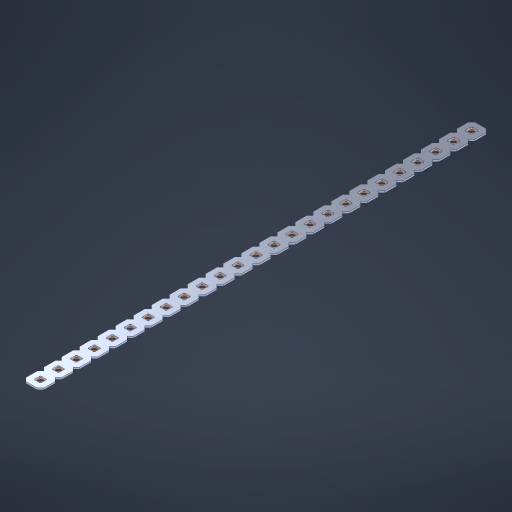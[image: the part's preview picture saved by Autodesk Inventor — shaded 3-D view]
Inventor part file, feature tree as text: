
AUTODESK INVENTOR PART (.ipt)
format: ipt  version: 2023 (Build 270158000, 158)  size: 579,072 bytes
history: native  units: in
note: dims shown in document units (in); Inventor stores cm internally (conversion verified against a paired STEP export)
features: other x26, extrude x24, sketch x2, pattern_linear x1
ambient origin geometry x8: Origin, YZ Plane, XZ Plane, XY Plane, X Axis, Y Axis, Z Axis, Center Point
bodies: Solid1 (feature_tree), Body (feature_tree)
feature tree (53):
  pattern_linear  "Rectangular Pattern1"  Spacing1=0.09in  [1 undecoded]
  sketch  "Sketch1"  dims[d1=0.5in]
  sketch  "Sketch2"  dims[d2=0.182in d3=0.09in d4=0.09in d5=0.09in d6=0.09in d7=0.09in d8=0.09in d9=0.09in d10=0.09in d11=0.02in d13=0.0in d14=0.172in d15=0.0625in d16=0.0in d19=0.5in d22=0.5in]
  other  "Srf1"
  other  "Srf126"
  other  "Srf127"
  other  "Srf128"
  other  "Srf129"
  other  "Srf130"
  other  "Srf131"
  other  "Srf250"
  other  "Srf251"
  other  "Srf252"
  other  "Srf253"
  other  "Srf254"
  other  "Srf255"
  other  "Srf256"
  other  "Srf257"
  other  "Srf258"
  other  "Srf259"
  other  "Srf260"
  other  "Srf261"
  other  "Srf262"
  other  "Srf263"
  other  "Srf264"
  other  "Srf265"
  other  "Srf266"
  other  "Srf267"
  other  "Circle"
  extrude  "ExtrusionSrf126"  Depth=0.09in
  extrude  "ExtrusionSrf127"  Depth=0.09in
  extrude  "ExtrusionSrf128"  Depth=0.09in
  extrude  "ExtrusionSrf129"  Depth=0.09in
  extrude  "ExtrusionSrf130"  Depth=0.09in
  extrude  "ExtrusionSrf131"  Depth=0.09in
  extrude  "ExtrusionSrf250"  Depth=0.09in
  extrude  "ExtrusionSrf251"  Depth=0.02in
  extrude  "ExtrusionSrf252"  TaperAngle=0.0deg  [1 undecoded]
  extrude  "ExtrusionSrf253"  Depth=0.5in
  extrude  "ExtrusionSrf254"  Depth=0.5in TaperAngle=0.0deg
  extrude  "ExtrusionSrf255"  Depth=0.5in
  extrude  "ExtrusionSrf256"  Depth=0.5in
  extrude  "ExtrusionSrf257"  [1 undecoded]
  extrude  "ExtrusionSrf258"  [1 undecoded]
  extrude  "ExtrusionSrf259"  [1 undecoded]
  extrude  "ExtrusionSrf260"  [1 undecoded]
  extrude  "ExtrusionSrf261"  [1 undecoded]
  extrude  "ExtrusionSrf262"  [1 undecoded]
  extrude  "ExtrusionSrf263"  [1 undecoded]
  extrude  "ExtrusionSrf264"  [1 undecoded]
  extrude  "ExtrusionSrf265"  [1 undecoded]
  extrude  "ExtrusionSrf266"  [1 undecoded]
  extrude  "ExtrusionSrf267"  [1 undecoded]
note: 13 required parameter values undecoded (feature->parameter linkage not recoverable at this tier; creation-order binding heuristic only, values carry confidence <= 0.55)
